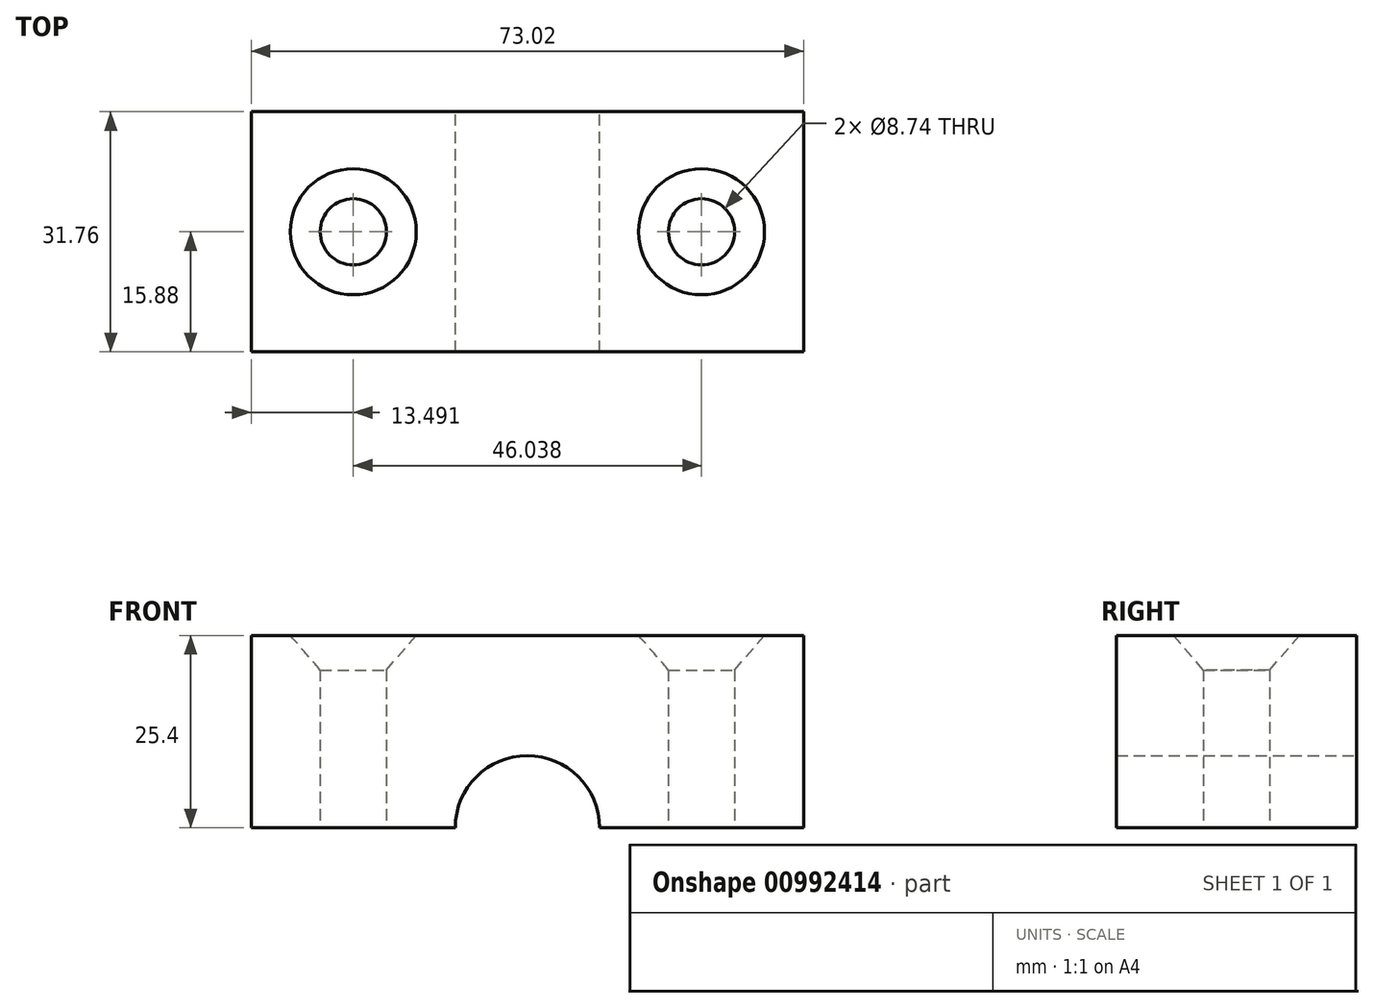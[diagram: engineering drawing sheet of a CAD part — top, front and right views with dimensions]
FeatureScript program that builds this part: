
annotation { "Feature Type Name" : "Feature", "Feature Type Description" : "" }
export const myFeature = defineFeature(function(context is Context, id is Id, definition is map)
    precondition{}
    {
        {
            var Q0;
            Q0=qCreatedBy(makeId("Top.planeOp"),FACE);
            var sketch = newSketch(context, id + "F0", { "sketchPlane" : qUnion([Q0])});
            skLineSegment(sketch, "E0.bottom", {"start": v(36.51, 15.88) * mm, "end": v(-36.51, 15.88) * mm});
            skLineSegment(sketch, "E0.top", {"start": v(36.51, -15.87) * mm, "end": v(-36.51, -15.87) * mm});
            skLineSegment(sketch, "E0.left", {"start": v(36.51, 15.88) * mm, "end": v(36.51, -15.87) * mm});
            skLineSegment(sketch, "E0.right", {"start": v(-36.51, 15.88) * mm, "end": v(-36.51, -15.87) * mm});
            skPoint(sketch, "E0.middle", {"position": v(0, 0) * mm});
            skLineSegment(sketch, "E1", {"start": v(0, 15.88) * mm, "end": v(-36.51, 15.88) * mm});
            skPoint(sketch, "E2", {"position": v(-23.02, 0) * mm});
            skPoint(sketch, "E3", {"position": v(23.02, 0) * mm});
            skSolve(sketch);
        }
        {
            var Q0;
            {var subQ0=sQuery(id+"F0.wireOp",EDGE,"E0.right");Q0=makeQuery(id+"F0.imprint","IMPRINT",FACE,{"disambiguationData":[TD([[makeQuery(id+"F0.imprint","IMPRINT",EDGE,{"derivedFrom":subQ0}),1.0]])]});}
            var Q1;
            {var subQ0=sQuery(id+"F0.wireOp",EDGE,"E0.left");Q1=makeQuery(id+"F0.imprint","IMPRINT",FACE,{"disambiguationData":[TD([[makeQuery(id+"F0.imprint","IMPRINT",EDGE,{"derivedFrom":subQ0}),-1.0]])]});}
            var Q2;
            {var subQ0=sQuery(id+"F0.wireOp",EDGE,"tr4BtByD-QJ4e-L8bX-ME5j-CdknIoFvLDKO");Q2=makeQuery(id+"F0.imprint","IMPRINT",FACE,{"disambiguationData":[TD([[makeQuery(id+"F0.imprint","IMPRINT",EDGE,{"derivedFrom":subQ0}),-1.0]])]});}
            var Q3;
            {var subQ0=sQuery(id+"F0.wireOp",EDGE,"tr4BtByD-QJ4e-L8bX-ME5j-CdknIoFvLDKO");Q3=makeQuery(id+"F0.imprint","IMPRINT",FACE,{"disambiguationData":[TD([[makeQuery(id+"F0.imprint","IMPRINT",EDGE,{"derivedFrom":subQ0}),1.0]])]});}
            extrude(context, id + "F1", {"entities" : qUnion([Q0, Q1, Q2, Q3]), "oppositeDirection" : true, "depth" : 25.4 * mm, "offsetDistance" : 25.4 * mm});
        }
        {
            var Q0;
            Q0=sQuery(id+"F0.wireOp",VERTEX,"E2");
            var Q1;
            Q1=sQuery(id+"F0.wireOp",VERTEX,"E3");
            var Q2;
            Q2=makeQuery(id+"F1.opExtrude","SWEPT_BODY",BODY,{"disambiguationData":[OSD([sQuery(id+"F0.wireOp",EDGE,"E0.bottom"),sQuery(id+"F0.wireOp",EDGE,"E0.top"),sQuery(id+"F0.wireOp",EDGE,"E0.left"),sQuery(id+"F0.wireOp",EDGE,"E0.right"),sQuery(id+"F0.wireOp",EDGE,"E1")])]});
            hole(context, id + "F2", {"style" : HoleStyle.C_SINK, "endStyle" : HoleEndStyle.BLIND, "standardTappedOrClearance" : lookupTablePath({ "fit" : "Normal (ASME)", "standard" : "ANSI", "size" : "5/16", "type" : "Clearance" }), "standardBlindInLast" : lookupTablePath({ "fit" : "Normal", "standard" : "ANSI", "engagement" : "75%", "pitch" : "18 tpi", "size" : "5/16", "type" : "Clearance & tapped" }), "holeDiameter" : 8.74 * mm, "cSinkDiameter" : 16.66 * mm, "cSinkAngle" : 82 * degree, "majorDiameter" : 7.94 * mm, "holeDepth" : 29.63 * mm, "isTappedThrough" : true, "tappedDepth" : 25.4 * mm, "tapClearance" : 3, "locations" : qUnion([Q0, Q1]), "scope" : qUnion([Q2]), "startStyle" : HoleStartStyle.SKETCH});
        }
        {
            var Q0;
            Q0=makeQuery(id+"F1.opExtrude","SWEPT_FACE",FACE,{"disambiguationData":[OSD([sQuery(id+"F0.wireOp",EDGE,"E0.top")])]});
            var sketch = newSketch(context, id + "F3", { "sketchPlane" : qUnion([Q0])});
            skPoint(sketch, "E4", {"position": v(0, -25.4) * mm});
            skSolve(sketch);
        }
        {
            var Q0;
            Q0=sQuery(id+"F3.wireOp",VERTEX,"E4");
            var Q1;
            Q1=makeQuery(id+"F1.opExtrude","SWEPT_BODY",BODY,{"disambiguationData":[OSD([sQuery(id+"F0.wireOp",EDGE,"E0.bottom"),sQuery(id+"F0.wireOp",EDGE,"E0.top"),sQuery(id+"F0.wireOp",EDGE,"E0.left"),sQuery(id+"F0.wireOp",EDGE,"E0.right"),sQuery(id+"F0.wireOp",EDGE,"E1")])]});
            hole(context, id + "F4", {"style" : HoleStyle.SIMPLE, "endStyle" : HoleEndStyle.THROUGH, "holeDiameter" : 19.05 * mm, "majorDiameter" : 6.35 * mm, "isTappedThrough" : true, "tappedDepth" : 25.4 * mm, "tapClearance" : 3, "locations" : qUnion([Q0]), "scope" : qUnion([Q1]), "startStyle" : HoleStartStyle.SKETCH});
        }
    });
